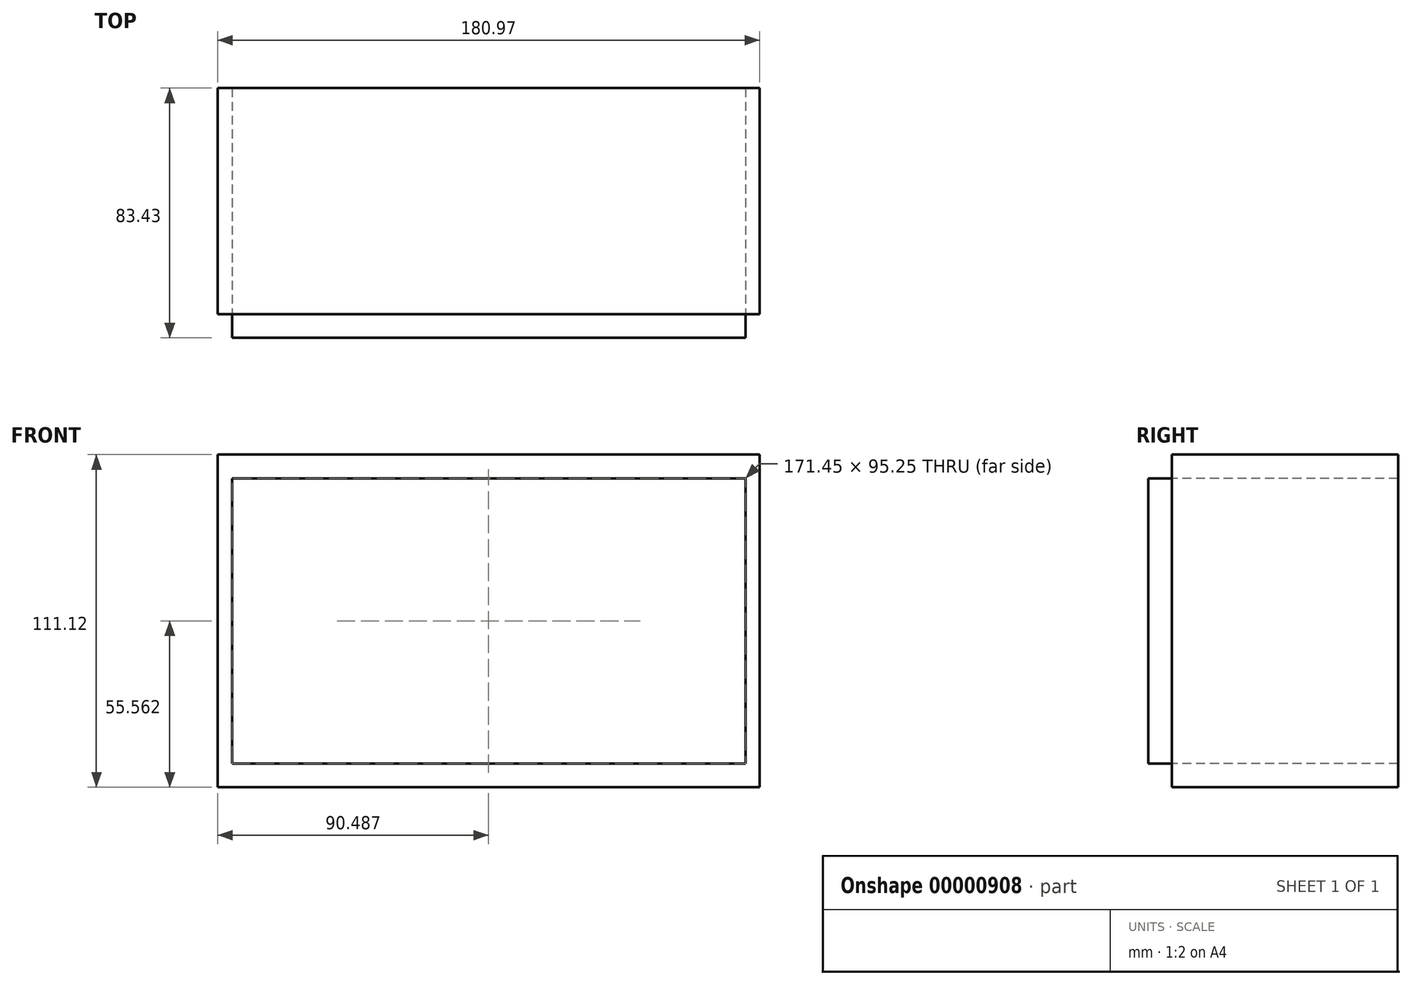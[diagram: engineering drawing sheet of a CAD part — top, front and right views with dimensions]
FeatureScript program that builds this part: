
annotation { "Feature Type Name" : "Feature", "Feature Type Description" : "" }
export const myFeature = defineFeature(function(context is Context, id is Id, definition is map)
    precondition{}
    {
        {
            var Q0;
            Q0=qCreatedBy(makeId("Front.planeOp"),FACE);
            var sketch = newSketch(context, id + "F0", { "sketchPlane" : qUnion([Q0])});
            skLineSegment(sketch, "E0.bottom", {"start": v(0, 0) * mm, "end": v(180.98, 0) * mm});
            skLineSegment(sketch, "E0.top", {"start": v(0, 111.13) * mm, "end": v(180.97, 111.13) * mm});
            skLineSegment(sketch, "E0.left", {"start": v(0, 0) * mm, "end": v(0, 111.13) * mm});
            skLineSegment(sketch, "E0.right", {"start": v(180.98, 0) * mm, "end": v(180.98, 111.13) * mm});
            skLineSegment(sketch, "E1.bottom", {"start": v(4.76, 7.94) * mm, "end": v(176.21, 7.94) * mm});
            skLineSegment(sketch, "E1.top", {"start": v(4.76, 103.19) * mm, "end": v(176.21, 103.19) * mm});
            skLineSegment(sketch, "E1.left", {"start": v(4.76, 7.94) * mm, "end": v(4.76, 103.19) * mm});
            skLineSegment(sketch, "E1.right", {"start": v(176.21, 7.94) * mm, "end": v(176.21, 103.19) * mm});
            skSolve(sketch);
        }
        {
            var Q0;
            Q0=makeQuery(id+"F0.imprint","IMPRINT",FACE,{"disambiguationData":[TD([[makeQuery(id+"F0.imprint","IMPRINT",EDGE,{"derivedFrom":sQuery(id+"F0.wireOp",EDGE,"E1.bottom")}),1.0]])]});
            extrude(context, id + "F1", {"entities" : qUnion([Q0]), "depth" : 7.94 * mm});
        }
        {
            var Q0;
            Q0=makeQuery(id+"F0.imprint","IMPRINT",FACE,{"disambiguationData":[TD([[makeQuery(id+"F0.imprint","IMPRINT",EDGE,{"derivedFrom":sQuery(id+"F0.wireOp",EDGE,"E0.bottom")}),1.0]])]});
            extrude(context, id + "F2", {"entities" : qUnion([Q0]), "operationType" : NewBodyOperationType.ADD, "oppositeDirection" : true, "depth" : 75.49 * mm});
        }
    });
